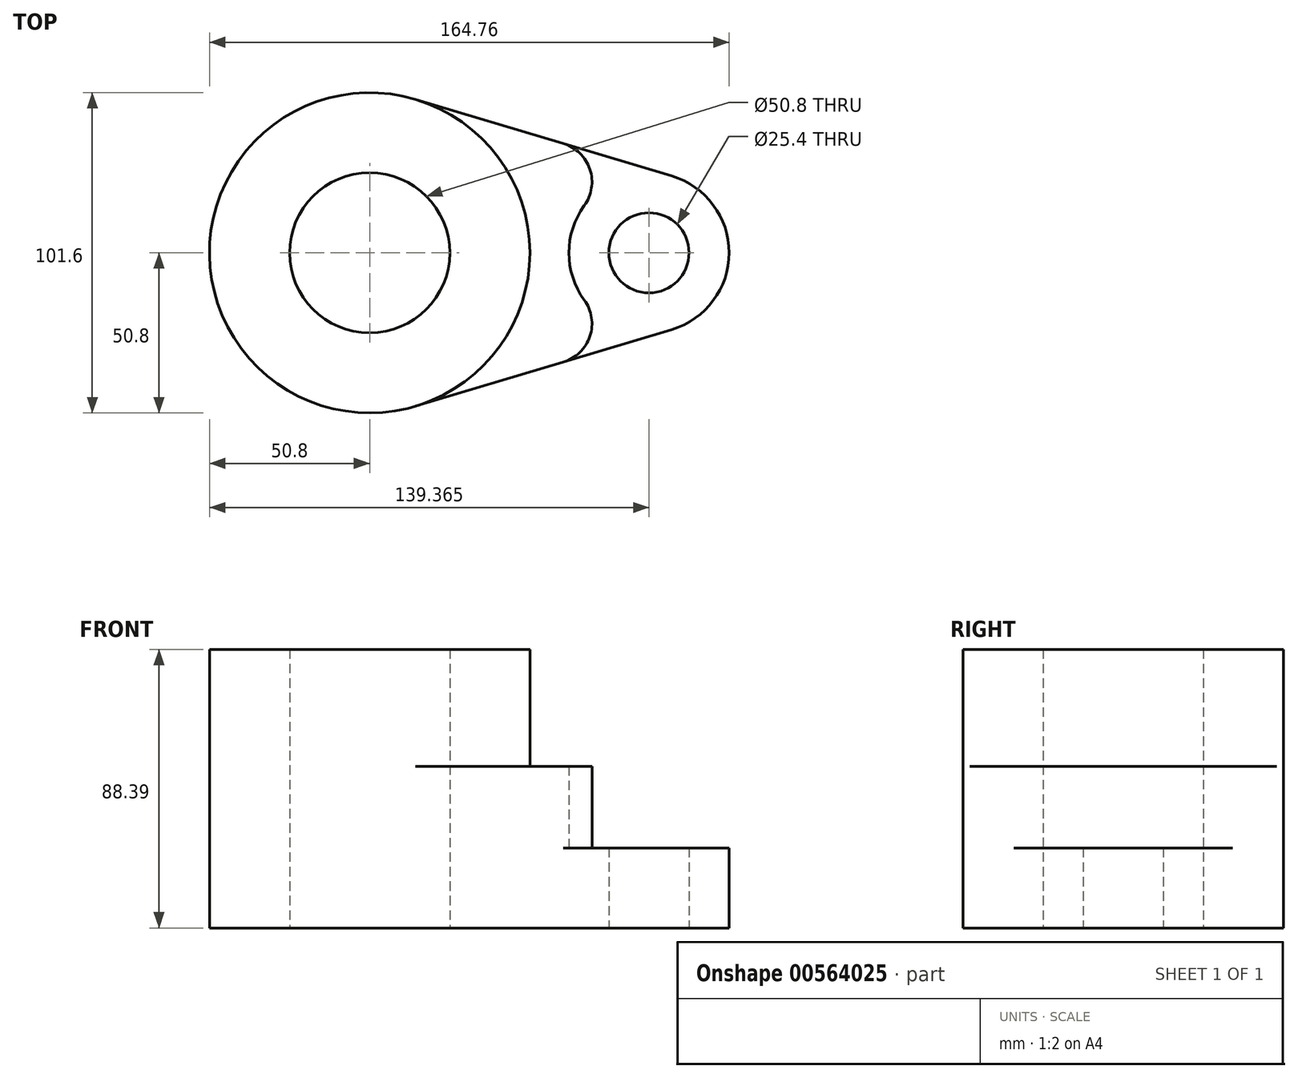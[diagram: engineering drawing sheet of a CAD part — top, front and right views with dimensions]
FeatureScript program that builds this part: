
annotation { "Feature Type Name" : "Feature", "Feature Type Description" : "" }
export const myFeature = defineFeature(function(context is Context, id is Id, definition is map)
    precondition{}
    {
        {
            var Q0;
            Q0=qCreatedBy(makeId("Top.planeOp"),FACE);
            var sketch = newSketch(context, id + "F0", { "sketchPlane" : qUnion([Q0])});
            skCircle(sketch, "E0", {"center": v(0, 0) * mm, "radius": 50.8 * mm});
            skCircle(sketch, "E1", {"center": v(0, 0) * mm, "radius": 25.4 * mm});
            skCircle(sketch, "E2", {"center": v(88.56, 0) * mm, "radius": 12.7 * mm});
            skCircle(sketch, "E3", {"center": v(88.56, 0) * mm, "radius": 25.4 * mm});
            skLineSegment(sketch, "E4", {"start": v(14.57, 48.67) * mm, "end": v(95.85, 24.33) * mm});
            skLineSegment(sketch, "E5", {"start": v(14.57, -48.67) * mm, "end": v(95.85, -24.33) * mm});
            skSolve(sketch);
        }
        {
            var Q0;
            Q0=makeQuery(id+"F0.imprint","IMPRINT",FACE,{"disambiguationData":[TD([[makeQuery(id+"F0.imprint","IMPRINT",EDGE,{"derivedFrom":sQuery(id+"F0.wireOp",EDGE,"E1")}),-1.0]])]});
            var Q1;
            {var subQ0=sQuery(id+"F0.wireOp",EDGE,"E4");Q1=makeQuery(id+"F0.imprint","IMPRINT",FACE,{"disambiguationData":[TD([[makeQuery(id+"F0.imprint","IMPRINT",EDGE,{"derivedFrom":subQ0}),-1.0]])]});}
            var Q2;
            Q2=makeQuery(id+"F0.imprint","IMPRINT",FACE,{"disambiguationData":[TD([[makeQuery(id+"F0.imprint","IMPRINT",EDGE,{"derivedFrom":sQuery(id+"F0.wireOp",EDGE,"E2")}),-1.0]])]});
            extrude(context, id + "F1", {"entities" : qUnion([Q0, Q1, Q2]), "depth" : 25.4 * mm, "offsetDistance" : 25.4 * mm});
        }
        {
            var Q0;
            Q0=makeQuery(id+"F0.imprint","IMPRINT",FACE,{"disambiguationData":[TD([[makeQuery(id+"F0.imprint","IMPRINT",EDGE,{"derivedFrom":sQuery(id+"F0.wireOp",EDGE,"E1")}),-1.0]])]});
            extrude(context, id + "F2", {"entities" : qUnion([Q0]), "operationType" : NewBodyOperationType.ADD, "depth" : 88.4 * mm, "offsetDistance" : 25.4 * mm});
        }
        {
            var Q0;
            {var subQ0=sQuery(id+"F0.wireOp",EDGE,"E4");Q0=makeQuery(id+"F0.imprint","IMPRINT",FACE,{"disambiguationData":[TD([[makeQuery(id+"F0.imprint","IMPRINT",EDGE,{"derivedFrom":subQ0}),-1.0]])]});}
            extrude(context, id + "F3", {"entities" : qUnion([Q0]), "operationType" : NewBodyOperationType.ADD, "depth" : 51.3 * mm, "offsetDistance" : 25.4 * mm});
        }
        {
            var Q0;
            Q0=makeQuery(id+"F3.opExtrude","SWEPT_EDGE",EDGE,{"disambiguationData":[OSD([sQuery(id+"F0.wireOp",EDGE,"E3"),sQuery(id+"F0.wireOp",EDGE,"E5")])]});
            var Q1;
            Q1=makeQuery(id+"F3.opExtrude","SWEPT_EDGE",EDGE,{"disambiguationData":[OSD([sQuery(id+"F0.wireOp",EDGE,"E3"),sQuery(id+"F0.wireOp",EDGE,"E4")])]});
            fillet(context, id + "F4", {"entities" : qUnion([Q0, Q1]), "radius" : 12.7 * mm, "tangentPropagation" : true, "allowEdgeOverflow" : false});
        }
    });
